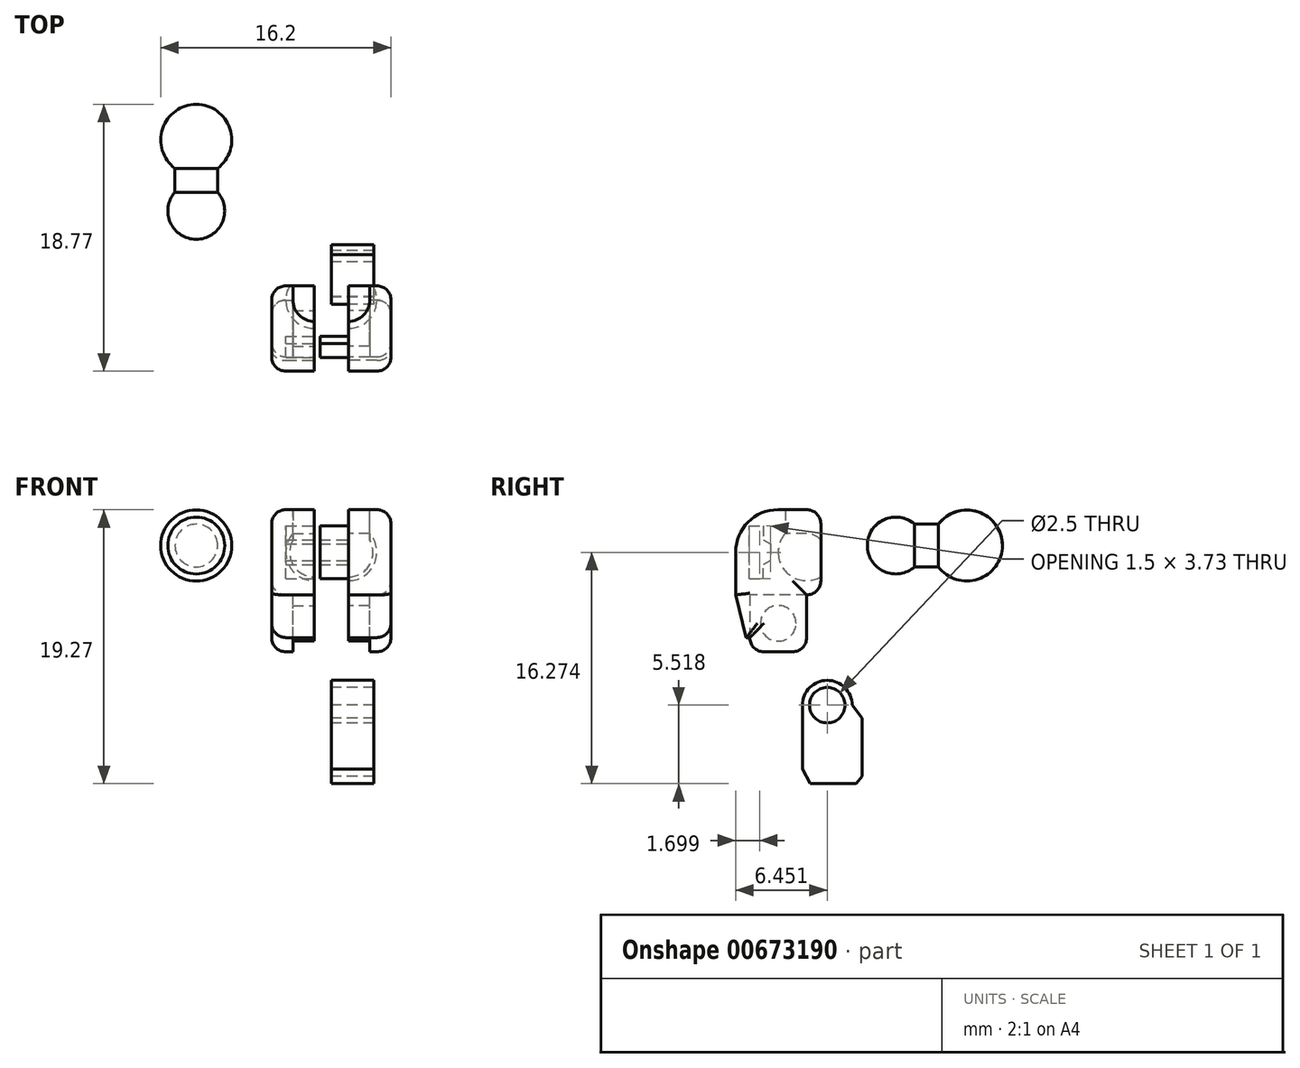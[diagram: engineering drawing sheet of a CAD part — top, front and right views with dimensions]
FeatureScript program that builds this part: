
annotation { "Feature Type Name" : "Feature", "Feature Type Description" : "" }
export const myFeature = defineFeature(function(context is Context, id is Id, definition is map)
    precondition{}
    {
        {
            var Q0;
            Q0=qCreatedBy(makeId("Right.planeOp"),FACE);
            var sketch = newSketch(context, id + "F0", { "sketchPlane" : qUnion([Q0])});
            skArc(sketch, "E0", {"start": v(2.5, 0) * mm, "mid": v(0.8, 2.37) * mm, "end": v(-2, 1.5) * mm});
            skLineSegment(sketch, "E1", {"start": v(0, 0) * mm, "end": v(0, 1.5) * mm, "construction": true});
            skLineSegment(sketch, "E2", {"start": v(0, 1.5) * mm, "end": v(-2, 1.5) * mm, "construction": true});
            skLineSegment(sketch, "E3", {"start": v(-2, 1.5) * mm, "end": v(-5, 1.5) * mm});
            skLineSegment(sketch, "E4", {"start": v(-5, 1.5) * mm, "end": v(-5, 0) * mm});
            skArc(sketch, "E5", {"start": v(-3.68, 1.5) * mm, "mid": v(-5.82, 1.82) * mm, "end": v(-7, 0) * mm});
            skLineSegment(sketch, "E6", {"start": v(2.5, 0) * mm, "end": v(-7, 0) * mm});
            skPoint(sketch, "E7.orphan", {"position": v(-5, -1.5) * mm});
            skSolve(sketch);
        }
        {
            var Q0;
            {var subQ3=sQuery(id+"F0.wireOp",EDGE,"E0");Q0=makeQuery(id+"F0.imprint","IMPRINT",FACE,{"disambiguationData":[TD([[makeQuery(id+"F0.imprint","IMPRINT",EDGE,{"derivedFrom":subQ3}),1.0]])]});}
            var Q1;
            {var subQ0=sQuery(id+"F0.wireOp",EDGE,"E4");Q1=makeQuery(id+"F0.imprint","IMPRINT",FACE,{"disambiguationData":[TD([[makeQuery(id+"F0.imprint","IMPRINT",EDGE,{"derivedFrom":subQ0}),-1.0]])]});}
            var Q2;
            Q2=sQuery(id+"F0.wireOp",EDGE,"E6");
            revolve(context, id + "F1", {"entities" : qUnion([Q0, Q1]), "axis" : qUnion([Q2]), "revolveType" : RevolveType.FULL});
        }
        {
            var Q0;
            Q0=qCreatedBy(makeId("Right.planeOp"),FACE);
            cPlane(context, id + "F2", {"entities" : qUnion([Q0]), "cplaneType" : CPlaneType.OFFSET, "offset" : 8.3 * mm, "width" : 150 * mm, "height" : 150 * mm});
        }
        {
            var Q0;
            Q0=qCreatedBy(id+"F2.planeOp",FACE);
            var sketch = newSketch(context, id + "F3", { "sketchPlane" : qUnion([Q0])});
            skLineSegment(sketch, "E8.bottom", {"start": v(-10.27, 2.52) * mm, "end": v(-16.27, 2.52) * mm});
            skLineSegment(sketch, "E8.top", {"start": v(-10.27, -3.48) * mm, "end": v(-16.27, -3.48) * mm});
            skLineSegment(sketch, "E8.left", {"start": v(-10.27, 2.52) * mm, "end": v(-10.27, -0.48) * mm});
            skArc(sketch, "E9", {"start": v(-13.27, -0.48) * mm, "mid": v(-11.27, -2.48) * mm, "end": v(-9.27, -0.48) * mm});
            skPoint(sketch, "E9.centerSnap0", {"position": v(-10.27, -0.48) * mm});
            skLineSegment(sketch, "E10", {"start": v(-9.27, -0.48) * mm, "end": v(-13.27, -0.48) * mm});
            skLineSegment(sketch, "E11.trimOffspring", {"start": v(-10.27, -2.2) * mm, "end": v(-10.27, -3.48) * mm});
            skLineSegment(sketch, "E12", {"start": v(-13.27, 2.52) * mm, "end": v(-13.27, -3.48) * mm, "construction": true});
            skLineSegment(sketch, "E13", {"start": v(-16.27, 2.52) * mm, "end": v(-16.27, -3.48) * mm});
            skArc(sketch, "E14.cCircle", {"start": v(-14.32, -1.34) * mm, "mid": v(-13.82, -0.48) * mm, "end": v(-14.32, 0.39) * mm, "construction": true});
            skLineSegment(sketch, "E14.2", {"start": v(-14.32, 0.39) * mm, "end": v(-13.82, 0.1) * mm});
            skLineSegment(sketch, "E14.3", {"start": v(-13.82, 0.1) * mm, "end": v(-13.82, -1.05) * mm});
            skLineSegment(sketch, "E14.4", {"start": v(-13.82, -1.05) * mm, "end": v(-14.32, -1.34) * mm});
            skPoint(sketch, "E14.0.midPoint", {"position": v(-15.82, -0.48) * mm});
            skLineSegment(sketch, "E15", {"start": v(-15.32, -1.34) * mm, "end": v(-15.32, -2.34) * mm});
            skLineSegment(sketch, "E16", {"start": v(-15.32, -2.34) * mm, "end": v(-14.32, -2.34) * mm});
            skPoint(sketch, "E16.endSnap0", {"position": v(-14.32, -1.34) * mm});
            skLineSegment(sketch, "E17", {"start": v(-14.32, -2.34) * mm, "end": v(-14.32, -1.34) * mm});
            skLineSegment(sketch, "E18.MirrorCS", {"start": v(-15.32, 1.39) * mm, "end": v(-14.32, 1.39) * mm});
            skLineSegment(sketch, "E19.MirrorCS", {"start": v(-15.32, 0.39) * mm, "end": v(-15.32, 1.39) * mm});
            skLineSegment(sketch, "E20.MirrorCS", {"start": v(-14.32, 1.39) * mm, "end": v(-14.32, 0.39) * mm});
            skLineSegment(sketch, "E21", {"start": v(-15.32, 0.39) * mm, "end": v(-15.32, -1.34) * mm});
            skPoint(sketch, "E22.orphan", {"position": v(-15.82, -1.05) * mm});
            skPoint(sketch, "E14.0.end.orphan", {"position": v(-15.82, 0.1) * mm});
            skPoint(sketch, "E23.orphan", {"position": v(-14.82, -1.63) * mm});
            skLineSegment(sketch, "E24", {"start": v(-16.27, -4.65) * mm, "end": v(-15.27, -4.65) * mm, "construction": true});
            skLineSegment(sketch, "E25", {"start": v(-15.27, -3.48) * mm, "end": v(-15.27, -7.48) * mm});
            skLineSegment(sketch, "E26", {"start": v(-15.27, -7.48) * mm, "end": v(-11.27, -7.48) * mm});
            skLineSegment(sketch, "E27", {"start": v(-11.27, -7.48) * mm, "end": v(-11.27, -3.48) * mm});
            skCircle(sketch, "E28", {"center": v(-13.27, -5.48) * mm, "radius": 1.25 * mm});
            skPoint(sketch, "E28.centerSnap0", {"position": v(-13.27, -7.48) * mm});
            skPoint(sketch, "E28.centerSnap1", {"position": v(-15.27, -5.48) * mm});
            skLineSegment(sketch, "E29", {"start": v(-10.27, -0.48) * mm, "end": v(-10.27, -2.2) * mm});
            skLineSegment(sketch, "E30", {"start": v(-15.52, -6.48) * mm, "end": v(-16.27, -3.48) * mm});
            skLineSegment(sketch, "E31", {"start": v(-15.52, -6.48) * mm, "end": v(-15.27, -6.48) * mm});
            skPoint(sketch, "E32.start.orphan", {"position": v(-16.04, -7.48) * mm});
            skSolve(sketch);
        }
        {
            var Q0;
            Q0=makeQuery(id+"F3.imprint","IMPRINT",FACE,{"disambiguationData":[TD([[makeQuery(id+"F3.imprint","IMPRINT",EDGE,{"derivedFrom":sQuery(id+"F3.wireOp",EDGE,"E8.bottom")}),1.0]])]});
            var Q1;
            Q1=makeQuery(id+"F3.imprint","IMPRINT",FACE,{"disambiguationData":[TD([[makeQuery(id+"F3.imprint","IMPRINT",EDGE,{"derivedFrom":sQuery(id+"F3.wireOp",EDGE,"E14.2")}),-1.0]])]});
            var Q2;
            Q2=makeQuery(id+"F3.imprint","IMPRINT",FACE,{"disambiguationData":[TD([[makeQuery(id+"F3.imprint","IMPRINT",EDGE,{"derivedFrom":sQuery(id+"F3.wireOp",EDGE,"E28")}),1.0]])]});
            var Q3;
            {var subQ1=sQuery(id+"F3.wireOp",EDGE,"E25");Q3=makeQuery(id+"F3.imprint","IMPRINT",FACE,{"disambiguationData":[TD([[makeQuery(id+"F3.imprint","IMPRINT",EDGE,{"derivedFrom":subQ1}),1.0]])]});}
            var Q4;
            {var subQ3=sQuery(id+"F3.wireOp",EDGE,"E29");Q4=makeQuery(id+"F3.imprint","IMPRINT",FACE,{"disambiguationData":[TD([[makeQuery(id+"F3.imprint","IMPRINT",EDGE,{"derivedFrom":subQ3}),-1.0]])]});}
            var Q5;
            {var subQ2=sQuery(id+"F3.wireOp",EDGE,"E25");Q5=makeQuery(id+"F3.imprint","IMPRINT",FACE,{"disambiguationData":[TD([[makeQuery(id+"F3.imprint","IMPRINT",EDGE,{"derivedFrom":subQ2}),-1.0]])]});}
            extrude(context, id + "F4", {"entities" : qUnion([Q0, Q1, Q2, Q3, Q4, Q5]), "oppositeDirection" : true, "depth" : 3 * mm});
        }
        {
            var Q0;
            {var subQ1=sQuery(id+"F3.wireOp",EDGE,"E25");Q0=makeQuery(id+"F3.imprint","IMPRINT",FACE,{"disambiguationData":[TD([[makeQuery(id+"F3.imprint","IMPRINT",EDGE,{"derivedFrom":subQ1}),1.0]])]});}
            var Q1;
            Q1=makeQuery(id+"F3.imprint","IMPRINT",FACE,{"disambiguationData":[TD([[makeQuery(id+"F3.imprint","IMPRINT",EDGE,{"derivedFrom":sQuery(id+"F3.wireOp",EDGE,"E14.2")}),-1.0]])]});
            extrude(context, id + "F5", {"entities" : qUnion([Q0, Q1]), "operationType" : NewBodyOperationType.REMOVE, "oppositeDirection" : true, "depth" : 1.5 * mm});
        }
        {
            var Q0;
            {var subQ3=sQuery(id+"F3.wireOp",EDGE,"E29");Q0=makeQuery(id+"F3.imprint","IMPRINT",FACE,{"disambiguationData":[TD([[makeQuery(id+"F3.imprint","IMPRINT",EDGE,{"derivedFrom":subQ3}),-1.0]])]});}
            var Q1;
            Q1=sQuery(id+"F3.wireOp",EDGE,"E10");
            revolve(context, id + "F6", {"operationType" : NewBodyOperationType.REMOVE, "entities" : qUnion([Q0]), "axis" : qUnion([Q1]), "revolveType" : RevolveType.FULL, "oppositeDirection" : true});
        }
        {
            var Q0;
            Q0=qCreatedBy(id+"F2.planeOp",FACE);
            cPlane(context, id + "F7", {"entities" : qUnion([Q0]), "cplaneType" : CPlaneType.OFFSET, "offset" : 1.2 * mm, "width" : 150 * mm, "height" : 150 * mm});
        }
        {
            var Q0;
            Q0=makeQuery(id+"F4.opExtrude","SWEPT_FACE",FACE,{"disambiguationData":[OSD([sQuery(id+"F3.wireOp",EDGE,"E8.left"),sQuery(id+"F3.wireOp",EDGE,"E11.trimOffspring"),sQuery(id+"F3.wireOp",EDGE,"E29")])]});
            var sketch = newSketch(context, id + "F8", { "sketchPlane" : qUnion([Q0])});
            skLineSegment(sketch, "E33", {"start": v(-6.8, 0.39) * mm, "end": v(-6.8, 2.52) * mm});
            skLineSegment(sketch, "E34", {"start": v(-6.8, 0.39) * mm, "end": v(-8.3, 0.39) * mm});
            skLineSegment(sketch, "E35", {"start": v(-8.3, 0.39) * mm, "end": v(-8.3, 1.26) * mm});
            skPoint(sketch, "E36.end.orphan", {"position": v(-6.8, 1.26) * mm});
            skSolve(sketch);
        }
        {
            var Q0;
            {var subQ0=sQuery(id+"F8.wireOp",EDGE,"E33");Q0=makeQuery(id+"F8.imprint","IMPRINT",FACE,{"disambiguationData":[TD([[makeQuery(id+"F8.imprint","IMPRINT",EDGE,{"derivedFrom":subQ0}),1.0]])]});}
            var Q1;
            {var subQ0=sQuery(id+"F8.wireOp",EDGE,"E34");Q1=makeQuery(id+"F8.imprint","IMPRINT",FACE,{"disambiguationData":[TD([[makeQuery(id+"F8.imprint","IMPRINT",EDGE,{"derivedFrom":subQ0}),-1.0]])]});}
            extrude(context, id + "F9", {"entities" : qUnion([Q0, Q1]), "operationType" : NewBodyOperationType.REMOVE, "oppositeDirection" : true, "depth" : 2.5 * mm});
        }
        {
            var Q0;
            Q0=makeQuery(id+"F9.boolean.opBoolean","COPY",EDGE,{"derivedFrom":makeQuery(id+"F9.opExtrude","CAP_EDGE",EDGE,{"disambiguationData":[OSD([sQuery(id+"F8.wireOp",EDGE,"E33")])],"isStart":false})});
            fillet(context, id + "F10", {"entities" : qUnion([Q0]), "radius" : 1.5 * mm, "tangentPropagation" : true, "allowEdgeOverflow" : false});
        }
        {
            var Q0;
            Q0=makeQuery(id+"F4.opExtrude","SWEPT_BODY",BODY,{"disambiguationData":[OSD([sQuery(id+"F3.wireOp",EDGE,"E8.bottom"),sQuery(id+"F3.wireOp",EDGE,"E8.top"),sQuery(id+"F3.wireOp",EDGE,"E8.left"),sQuery(id+"F3.wireOp",EDGE,"E11.trimOffspring"),sQuery(id+"F3.wireOp",EDGE,"E13"),sQuery(id+"F3.wireOp",EDGE,"E25"),sQuery(id+"F3.wireOp",EDGE,"E26"),sQuery(id+"F3.wireOp",EDGE,"E27"),sQuery(id+"F3.wireOp",EDGE,"E29"),sQuery(id+"F3.wireOp",EDGE,"E30"),sQuery(id+"F3.wireOp",EDGE,"E31")])]});
            var Q1;
            Q1=qCreatedBy(id+"F7.planeOp",FACE);
            mirror(context, id + "F11", {"entities" : qUnion([Q0]), "mirrorPlane" : qUnion([Q1])});
        }
        {
            var Q0;
            Q0=makeQuery(id+"F11.opPattern","COPY",FACE,{"derivedFrom":makeQuery(id+"F5.boolean.opBoolean","COPY",FACE,{"derivedFrom":makeQuery(id+"F5.opExtrude","CAP_FACE",FACE,{"disambiguationData":[OSD([sQuery(id+"F3.wireOp",EDGE,"E14.2"),sQuery(id+"F3.wireOp",EDGE,"E14.3"),sQuery(id+"F3.wireOp",EDGE,"E14.4"),sQuery(id+"F3.wireOp",EDGE,"E15"),sQuery(id+"F3.wireOp",EDGE,"E16"),sQuery(id+"F3.wireOp",EDGE,"E17"),sQuery(id+"F3.wireOp",EDGE,"E18.MirrorCS"),sQuery(id+"F3.wireOp",EDGE,"E19.MirrorCS"),sQuery(id+"F3.wireOp",EDGE,"E20.MirrorCS"),sQuery(id+"F3.wireOp",EDGE,"E21")])],"isStart":false})}),"instanceName":"1"});
            extrude(context, id + "F12", {"entities" : qUnion([Q0]), "operationType" : NewBodyOperationType.ADD, "depth" : 3.5 * mm});
        }
        {
            var Q0;
            Q0=makeQuery(id+"F5.boolean.opBoolean","COPY",FACE,{"derivedFrom":makeQuery(id+"F5.opExtrude","CAP_FACE",FACE,{"disambiguationData":[OSD([sQuery(id+"F3.wireOp",EDGE,"E14.2"),sQuery(id+"F3.wireOp",EDGE,"E14.3"),sQuery(id+"F3.wireOp",EDGE,"E14.4"),sQuery(id+"F3.wireOp",EDGE,"E15"),sQuery(id+"F3.wireOp",EDGE,"E16"),sQuery(id+"F3.wireOp",EDGE,"E17"),sQuery(id+"F3.wireOp",EDGE,"E18.MirrorCS"),sQuery(id+"F3.wireOp",EDGE,"E19.MirrorCS"),sQuery(id+"F3.wireOp",EDGE,"E20.MirrorCS"),sQuery(id+"F3.wireOp",EDGE,"E21")])],"isStart":false})});
            extrude(context, id + "F13", {"entities" : qUnion([Q0]), "operationType" : NewBodyOperationType.REMOVE, "oppositeDirection" : true, "depth" : .5 * mm});
        }
        {
            var Q0;
            Q0=makeQuery(id+"F4.opExtrude","CAP_FACE",FACE,{"disambiguationData":[OSD([sQuery(id+"F3.wireOp",EDGE,"E8.bottom"),sQuery(id+"F3.wireOp",EDGE,"E8.top"),sQuery(id+"F3.wireOp",EDGE,"E8.left"),sQuery(id+"F3.wireOp",EDGE,"E11.trimOffspring"),sQuery(id+"F3.wireOp",EDGE,"E13"),sQuery(id+"F3.wireOp",EDGE,"E25"),sQuery(id+"F3.wireOp",EDGE,"E26"),sQuery(id+"F3.wireOp",EDGE,"E27"),sQuery(id+"F3.wireOp",EDGE,"E29"),sQuery(id+"F3.wireOp",EDGE,"E30"),sQuery(id+"F3.wireOp",EDGE,"E31")])],"isStart":false});
            var Q1;
            Q1=makeQuery(id+"F11.opPattern","COPY",FACE,{"derivedFrom":makeQuery(id+"F4.opExtrude","CAP_FACE",FACE,{"disambiguationData":[OSD([sQuery(id+"F3.wireOp",EDGE,"E8.bottom"),sQuery(id+"F3.wireOp",EDGE,"E8.top"),sQuery(id+"F3.wireOp",EDGE,"E8.left"),sQuery(id+"F3.wireOp",EDGE,"E11.trimOffspring"),sQuery(id+"F3.wireOp",EDGE,"E13"),sQuery(id+"F3.wireOp",EDGE,"E25"),sQuery(id+"F3.wireOp",EDGE,"E26"),sQuery(id+"F3.wireOp",EDGE,"E27"),sQuery(id+"F3.wireOp",EDGE,"E29"),sQuery(id+"F3.wireOp",EDGE,"E30"),sQuery(id+"F3.wireOp",EDGE,"E31")])],"isStart":false}),"instanceName":"1"});
            var Q2;
            Q2=makeQuery(id+"F4.opExtrude","SWEPT_EDGE",EDGE,{"disambiguationData":[OSD([sQuery(id+"F3.wireOp",EDGE,"E8.bottom"),sQuery(id+"F3.wireOp",EDGE,"E8.left")])]});
            var Q3;
            Q3=makeQuery(id+"F11.opPattern","COPY",EDGE,{"derivedFrom":makeQuery(id+"F4.opExtrude","SWEPT_EDGE",EDGE,{"disambiguationData":[OSD([sQuery(id+"F3.wireOp",EDGE,"E8.bottom"),sQuery(id+"F3.wireOp",EDGE,"E8.left")])]}),"instanceName":"1"});
            var Q4;
            Q4=makeQuery(id+"F11.opPattern","COPY",EDGE,{"derivedFrom":makeQuery(id+"F4.opExtrude","SWEPT_EDGE",EDGE,{"disambiguationData":[OSD([sQuery(id+"F3.wireOp",EDGE,"E8.top"),sQuery(id+"F3.wireOp",EDGE,"E11.trimOffspring")])]}),"instanceName":"1"});
            var Q5;
            Q5=makeQuery(id+"F4.opExtrude","SWEPT_EDGE",EDGE,{"disambiguationData":[OSD([sQuery(id+"F3.wireOp",EDGE,"E8.top"),sQuery(id+"F3.wireOp",EDGE,"E11.trimOffspring")])]});
            var Q6;
            Q6=makeQuery(id+"F4.opExtrude","SWEPT_EDGE",EDGE,{"disambiguationData":[OSD([sQuery(id+"F3.wireOp",EDGE,"E25"),sQuery(id+"F3.wireOp",EDGE,"E26")])]});
            var Q7;
            Q7=makeQuery(id+"F4.opExtrude","SWEPT_EDGE",EDGE,{"disambiguationData":[OSD([sQuery(id+"F3.wireOp",EDGE,"E26"),sQuery(id+"F3.wireOp",EDGE,"E27")])]});
            var Q8;
            Q8=makeQuery(id+"F11.opPattern","COPY",EDGE,{"derivedFrom":makeQuery(id+"F4.opExtrude","SWEPT_EDGE",EDGE,{"disambiguationData":[OSD([sQuery(id+"F3.wireOp",EDGE,"E26"),sQuery(id+"F3.wireOp",EDGE,"E27")])]}),"instanceName":"1"});
            var Q9;
            Q9=makeQuery(id+"F11.opPattern","COPY",EDGE,{"derivedFrom":makeQuery(id+"F4.opExtrude","SWEPT_EDGE",EDGE,{"disambiguationData":[OSD([sQuery(id+"F3.wireOp",EDGE,"E25"),sQuery(id+"F3.wireOp",EDGE,"E26")])]}),"instanceName":"1"});
            fillet(context, id + "F14", {"entities" : qUnion([Q0, Q1, Q2, Q3, Q4, Q5, Q6, Q7, Q8, Q9]), "radius" : 1 * mm, "tangentPropagation" : true, "allowEdgeOverflow" : false});
        }
        {
            var Q0;
            Q0=qCreatedBy(id+"F7.planeOp",FACE);
            var sketch = newSketch(context, id + "F15", { "sketchPlane" : qUnion([Q0])});
            skCircle(sketch, "E37", {"center": v(-9.82, -11.23) * mm, "radius": 1.25 * mm});
            skCircle(sketch, "E38", {"center": v(-9.82, -11.23) * mm, "radius": 1.75 * mm});
            skLineSegment(sketch, "E39", {"start": v(-11.57, -11.23) * mm, "end": v(-11.57, -14.73) * mm});
            skLineSegment(sketch, "E40", {"start": v(-11.57, -14.73) * mm, "end": v(-11.02, -15.75) * mm});
            skLineSegment(sketch, "E41", {"start": v(-11.02, -15.75) * mm, "end": v(-7.78, -15.75) * mm});
            skLineSegment(sketch, "E42", {"start": v(-7.78, -15.75) * mm, "end": v(-7.37, -15.24) * mm});
            skLineSegment(sketch, "E43", {"start": v(-7.37, -12.15) * mm, "end": v(-8.07, -11.23) * mm});
            skLineSegment(sketch, "E44", {"start": v(-7.37, -15.24) * mm, "end": v(-7.37, -12.15) * mm});
            skPoint(sketch, "E45.orphan", {"position": v(-6.95, -14.73) * mm});
            skSolve(sketch);
        }
        {
            var Q0;
            Q0=qSketchRegion(id+"F15",true);
            extrude(context, id + "F16", {"entities" : qUnion([Q0]), "depth" : 3 * mm});
        }
        {
            var Q0;
            Q0=makeQuery(id+"F16.opExtrude","SWEPT_FACE",FACE,{"disambiguationData":[OSD([sQuery(id+"F15.wireOp",EDGE,"E41")])]});
            var Q1;
            Q1=makeQuery(id+"F16.opExtrude","SWEPT_FACE",FACE,{"disambiguationData":[OSD([sQuery(id+"F15.wireOp",EDGE,"E40")])]});
            var Q2;
            Q2=makeQuery(id+"F16.opExtrude","SWEPT_FACE",FACE,{"disambiguationData":[OSD([sQuery(id+"F15.wireOp",EDGE,"E42")])]});
            extrude(context, id + "F17", {"entities" : qUnion([Q0, Q1, Q2]), "operationType" : NewBodyOperationType.ADD, "depth" : 1 * mm});
        }
        {
            var Q0;
            Q0=makeQuery(id+"F4.opExtrude","SWEPT_EDGE",EDGE,{"disambiguationData":[OSD([sQuery(id+"F3.wireOp",EDGE,"E8.bottom"),sQuery(id+"F3.wireOp",EDGE,"E13")])]});
            var Q1;
            Q1=makeQuery(id+"F11.opPattern","COPY",EDGE,{"derivedFrom":makeQuery(id+"F4.opExtrude","SWEPT_EDGE",EDGE,{"disambiguationData":[OSD([sQuery(id+"F3.wireOp",EDGE,"E8.bottom"),sQuery(id+"F3.wireOp",EDGE,"E13")])]}),"instanceName":"1"});
            fillet(context, id + "F18", {"entities" : qUnion([Q0, Q1]), "radius" : 3 * mm, "tangentPropagation" : true, "allowEdgeOverflow" : false});
        }
    });
